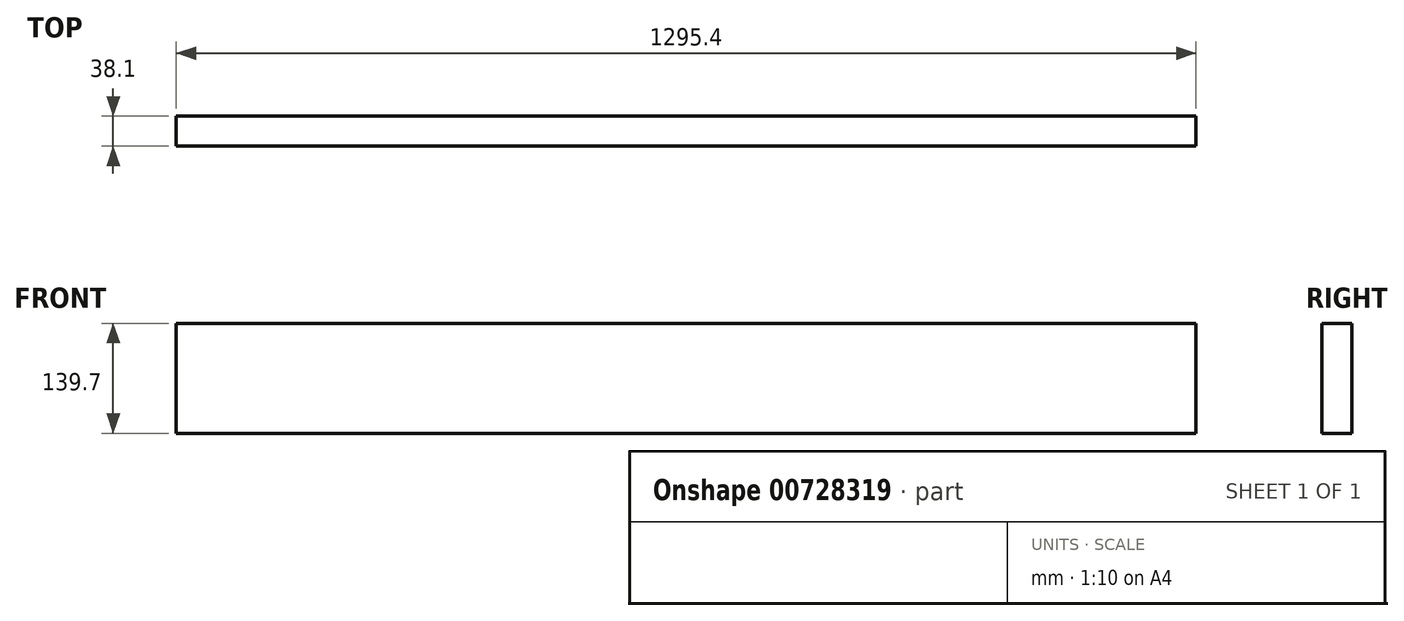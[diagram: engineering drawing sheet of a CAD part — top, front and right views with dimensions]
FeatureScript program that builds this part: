
annotation { "Feature Type Name" : "Feature", "Feature Type Description" : "" }
export const myFeature = defineFeature(function(context is Context, id is Id, definition is map)
    precondition{}
    {
        {
            var Q0;
            Q0=qCreatedBy(makeId("Front.planeOp"),FACE);
            var sketch = newSketch(context, id + "F0", { "sketchPlane" : qUnion([Q0])});
            skLineSegment(sketch, "E0.bottom", {"start": v(-647.7, -69.85) * mm, "end": v(647.7, -69.85) * mm});
            skLineSegment(sketch, "E0.top", {"start": v(-647.7, 69.85) * mm, "end": v(647.7, 69.85) * mm});
            skLineSegment(sketch, "E0.left", {"start": v(-647.7, -69.85) * mm, "end": v(-647.7, 69.85) * mm});
            skLineSegment(sketch, "E0.right", {"start": v(647.7, -69.85) * mm, "end": v(647.7, 69.85) * mm});
            skPoint(sketch, "E0.middle", {"position": v(0, 0) * mm});
            skSolve(sketch);
        }
        {
            var Q0;
            Q0=qSketchRegion(id+"F0",true);
            extrude(context, id + "F1", {"entities" : qUnion([Q0]), "depth" : 38.1 * mm});
        }
    });
